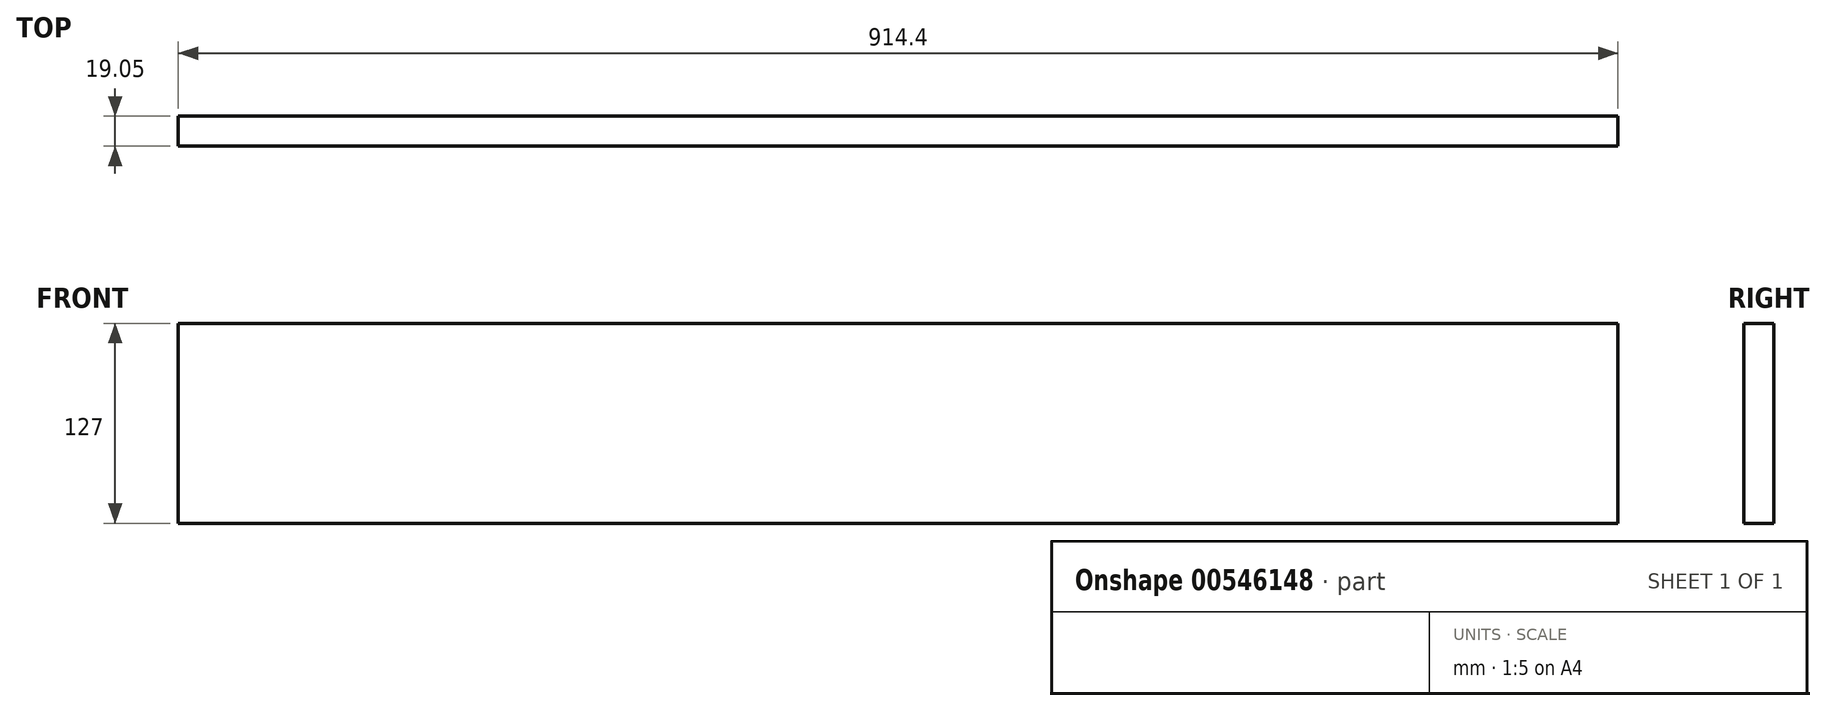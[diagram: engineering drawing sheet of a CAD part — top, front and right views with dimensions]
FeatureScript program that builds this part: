
annotation { "Feature Type Name" : "Feature", "Feature Type Description" : "" }
export const myFeature = defineFeature(function(context is Context, id is Id, definition is map)
    precondition{}
    {
        {
            var Q0;
            Q0=qCreatedBy(makeId("Front.planeOp"),FACE);
            var sketch = newSketch(context, id + "F0", { "sketchPlane" : qUnion([Q0])});
            skLineSegment(sketch, "E0.bottom", {"start": v(457.2, 63.5) * mm, "end": v(-457.2, 63.5) * mm});
            skLineSegment(sketch, "E0.top", {"start": v(457.2, -63.5) * mm, "end": v(-457.2, -63.5) * mm});
            skLineSegment(sketch, "E0.left", {"start": v(457.2, 63.5) * mm, "end": v(457.2, -63.5) * mm});
            skLineSegment(sketch, "E0.right", {"start": v(-457.2, 63.5) * mm, "end": v(-457.2, -63.5) * mm});
            skPoint(sketch, "E0.middle", {"position": v(0, 0) * mm});
            skSolve(sketch);
        }
        {
            var Q0;
            Q0 = qSketchRegion(id + "F0", true);
            extrude(context, id + "F1", {"entities" : qUnion([Q0]), "depth" : 19.05 * mm, "offsetDistance" : 25.4 * mm});
        }
    });
